# Revit family: VIESSMANN - Vitocrossal 300 CT3U
name_source: partatom
category: Wyposażenie mechaniczne
revit_build: Autodesk Revit 2017 (Build: 20160720_1515(x64)
units: mm (PartAtom-declared; Revit-internal decimal feet)

## family parameters
Numer OmniClass = 23.15.30.27.21
Oparty na płaszczyźnie roboczej = Nie
Punkt obliczania pomieszczeń = Nie
Tnij formami wycięć po wczytaniu = Tak
Typ części = Normalny
Tytuł OmniClass = Gas Tanks and Gasholders
Współdzielony = Nie
Wymiar okrągłego złącza = Użyj średnicy
Zawsze pionowo = Tak

## types (3) — shared parameters
Autor = https://www.archispace.pl
Ciśnienie na przyłączu gazu = 2 kPa
Częstotliwość = 50 Hz
Dop. ciśnienie robocze = 0.6 MPa
Dop. temperatura na zasilaniu (=temperatura progowa) = 110 °C
Dop. temperatura robocza = 95 °C
Długość palnika = 632 mm
Długość z pokrywą palnika = 653 mm  [stored 2.14239 ft]
Korpus kotła - szerokość bez drzwi kotła = 805 mm  [stored 2.64108 ft]
Korpus kotła - szerokość z drzwiami kotła = 845 mm  [stored 2.77231 ft]
Korpus kotła - wysokość = 1942 mm  [stored 6.37139 ft]
Liczba biegunów = 1
Mufa R1/2 do dodatkowych regulatorów = 1/2"
Mufa Rp - do ogranicznika ciśnienia = 1/2"
Napięcie zasilania = 230 V
Numer identyfikacyjny produktu = CE-0085AQ0257
Opis = Gazowy kocioł grzewczy
Opis indeksowy = CE-0085AQ0257
Opory przepływu = 0.0 MPa
PN 6 DN - powrót do kotła = 100 mm  [stored 0.328084 ft]
PN 6 DN - powrót do kotła 2 = 80.00 mm
PN 6 DN - zasilanie z kotła = 100 mm  [stored 0.328084 ft]
Parametry produktu wg. EnEV - sprawność znormalizowana przy temperaturze w systemie grzewczym wyn. 40/30°C = do 98 (Hs)
Parametry produktu wg. EnEV - sprawność znormalizowana przy temperaturze w systemie grzewczym wyn. 75/60°C = do 95 (Hs)
Parametry spalin - dyspozycyjne ciśnienie tłoczenia na króćcu spalin = 0.0 MPa
Parametry spalin - przy obciążeniu częściowym (przy temp. wody na powrocie wyn. 30°C) = 30 °C
Parametry spalin - przy znamionowej mocy cieplnej (przy temp. wody na powrocie wyn. 30°C) = 45 °C
Parametry spalin - przy znamionowej mocy cieplnej (przy temp. wody na powrocie wyn. 60°C) = 70 °C
Poziom mocy akustycznej - 1m przed kotłem (obciążenie pełne/częściowe) = <70/<55 dB(A)
Poziom mocy akustycznej - w rurze spalin (obciążenie pełne) = <98 - 105 dB(A)
Producent = Viessmann Sp.z.o.o.
Przyłącze spalin = 250 mm  [stored 0.82021 ft]
Przyłącze zabezpieczające (zawór bezpieczeństwa) = 1 1/2"
Spust = 1"
Spust kondensatu kolektor spalin = 32.00 mm
Spust kondensatu syfon = 20.00 mm
Szerokość całkowita = 1221 mm  [stored 4.00591 ft]
Szerokość fundamentu = 900 mm  [stored 2.95276 ft]
Szerokość palnika = 844 mm  [stored 2.76903 ft]
URL = https://www.viessmann-projektant.pl
Viessmann Kolor 1 = Viessmann Kolor 1
Viessmann Kolor 2 = Viessmann Kolor 2
Viessmann Kolor 3 = Viessmann Kolor 3
Współczynnik mocy = 1
Wykonanie palnika = Wbudowany Modulowany
Wysokość całkowita = 1987 mm  [stored 6.51903 ft]
Wysokość fundamentu = 100 mm  [stored 0.328084 ft]
Wysokość palnika = 935 mm  [stored 3.06759 ft]

## per-type parameters (varying)
- CT3U 500kW: Długość całkowita=1800 mm  [stored 5.90551 ft]; Długość całkowita palnika=967 mm  [stored 3.17257 ft]; Długość fundamentu=1300 mm  [stored 4.26509 ft]; Korpus kotła - długość=1295 mm; Masa - korpus kotła=645.00 kg; Masa - palnik z armaturą uniwersalną i pokrywą palnika=48.00 kg; Masa całkowita=795.00 kg; Moc cieplna palnika dolna=158 kW; Moc cieplna palnika górna=474 kW; Moc nominalna=500 kW; Model=Gazowy kocioł kondensacyjny Viessmann Vitocrossal 300 CT3U 500kW / Gas condensing boiler Viessmann Vitocrossal 300 CT3U 500kW; Parametry spalin - masowe natężenie przepływu w przypadku gazu ziemnego przy obciążeniu częściowym=240 kg/h; Parametry spalin - masowe natężenie przepływu w przypadku gazu ziemnego przy znamionowej mocy cieplnej=719 kg/h; Pobór mocy elektrycznej - przy dolnej mocy cieplnej=85 W; Pobór mocy elektrycznej - przy górnej mocy cieplnej=620 W; Pojemność wodna kotła=325.0 L; Przepływ maksymalny=21.60 m³/h; Straty energii dyżurnej qB,70=0.24 %; Typ palnika=VM IV-2; Wartości na przyłączu (w odniesieniu do maks. obciążenia) - gaz ziemny GZ-50/G20=16.7 do 50.2 m3/h; Wartości na przyłączu (w odniesieniu do maks. obciążenia) - gaz ziemny GZ41,5/G27=19.4 do 58.3 m3/h; Zakres znamionowego obciążenia cieplnego Qn=158 do 474 kW; Zakres znamionowej mocy cieplnej przy Tv/Tr 50/30°C=168 do 500 kW; Zakres znamionowej mocy cieplnej przy Tv/Tr 80/60°C=153 do 460 kW; a=1295 mm; b=1800 mm  [stored 5.90551 ft]; b-a=505 mm  [stored 1.65682 ft]
- CT3U 630kW: Długość całkowita=1960 mm  [stored 6.43045 ft]; Długość całkowita palnika=1027 mm  [stored 3.36942 ft]; Długość fundamentu=1500 mm  [stored 4.92126 ft]; Korpus kotła - długość=1450 mm  [stored 4.75722 ft]; Masa - korpus kotła=755.00 kg; Masa - palnik z armaturą uniwersalną i pokrywą palnika=50.00 kg; Masa całkowita=935.00 kg; Moc cieplna palnika dolna=198 kW; Moc cieplna palnika górna=593 kW; Moc nominalna=630 kW; Model=Gazowy kocioł kondensacyjny Viessmann Vitocrossal 300 CT3U 630kW / Gas condensing boiler Viessmann Vitocrossal 300 CT3U 630kW; Parametry spalin - masowe natężenie przepływu w przypadku gazu ziemnego przy obciążeniu częściowym=300 kg/h; Parametry spalin - masowe natężenie przepływu w przypadku gazu ziemnego przy znamionowej mocy cieplnej=900 kg/h; Pobór mocy elektrycznej - przy dolnej mocy cieplnej=95 W; Pobór mocy elektrycznej - przy górnej mocy cieplnej=880 W; Pojemność wodna kotła=406.0 L; Przepływ maksymalny=27.22 m³/h; Straty energii dyżurnej qB,70=0.23 %; Typ palnika=VM IV-3; Wartości na przyłączu (w odniesieniu do maks. obciążenia) - gaz ziemny GZ-50/G20=21.0 do 62.8 m3/h; Wartości na przyłączu (w odniesieniu do maks. obciążenia) - gaz ziemny GZ41,5/G27=24.4 do 73.0 m3/h; Zakres znamionowego obciążenia cieplnego Qn=148 do 593 kW; Zakres znamionowej mocy cieplnej przy Tv/Tr 50/30°C=209 do 630 kW; Zakres znamionowej mocy cieplnej przy Tv/Tr 80/60°C=192 do 575 kW; a=1450 mm  [stored 4.75722 ft]; b=1960 mm  [stored 6.43045 ft]; b-a=510 mm
- CT3U 400kW: Długość całkowita=1725 mm  [stored 5.65945 ft]; Długość całkowita palnika=927 mm  [stored 3.04134 ft]; Długość fundamentu=1250 mm  [stored 4.10105 ft]; Korpus kotła - długość=1220 mm  [stored 4.00262 ft]; Masa - korpus kotła=600.00 kg; Masa - palnik z armaturą uniwersalną i pokrywą palnika=41.00 kg; Masa całkowita=740.00 kg; Moc cieplna palnika dolna=127 kW; Moc cieplna palnika górna=381 kW; Moc nominalna=400 kW; Model=Gazowy kocioł kondensacyjny Viessmann Vitocrossal 300 CT3U 400kW / Gas condensing boiler Viessmann Vitocrossal 300 CT3U 400kW; Parametry spalin - masowe natężenie przepływu w przypadku gazu ziemnego przy obciążeniu częściowym=193 kg/h; Parametry spalin - masowe natężenie przepływu w przypadku gazu ziemnego przy znamionowej mocy cieplnej=578 kg/h; Pobór mocy elektrycznej - przy dolnej mocy cieplnej=80 W; Pobór mocy elektrycznej - przy górnej mocy cieplnej=575 W; Pojemność wodna kotła=261.0 L; Przepływ maksymalny=17.28 m³/h; Straty energii dyżurnej qB,70=0.25 %; Typ palnika=VM IV-1; Wartości na przyłączu (w odniesieniu do maks. obciążenia) - gaz ziemny GZ-50/G20=13.4 do 40.3 m3/h; Wartości na przyłączu (w odniesieniu do maks. obciążenia) - gaz ziemny GZ41,5/G27=15.6 do 46.9 m3/h; Zakres znamionowego obciążenia cieplnego Qn=127 do 381 kW; Zakres znamionowej mocy cieplnej przy Tv/Tr 50/30°C=135 do 400 kW; Zakres znamionowej mocy cieplnej przy Tv/Tr 80/60°C=123 do 370 kW; a=1220 mm  [stored 4.00262 ft]; b=1725 mm  [stored 5.65945 ft]; b-a=505 mm  [stored 1.65682 ft]

note: [stored X ft] marks values corroborated as IEEE doubles in the binary element streams (Revit-internal decimal feet)
